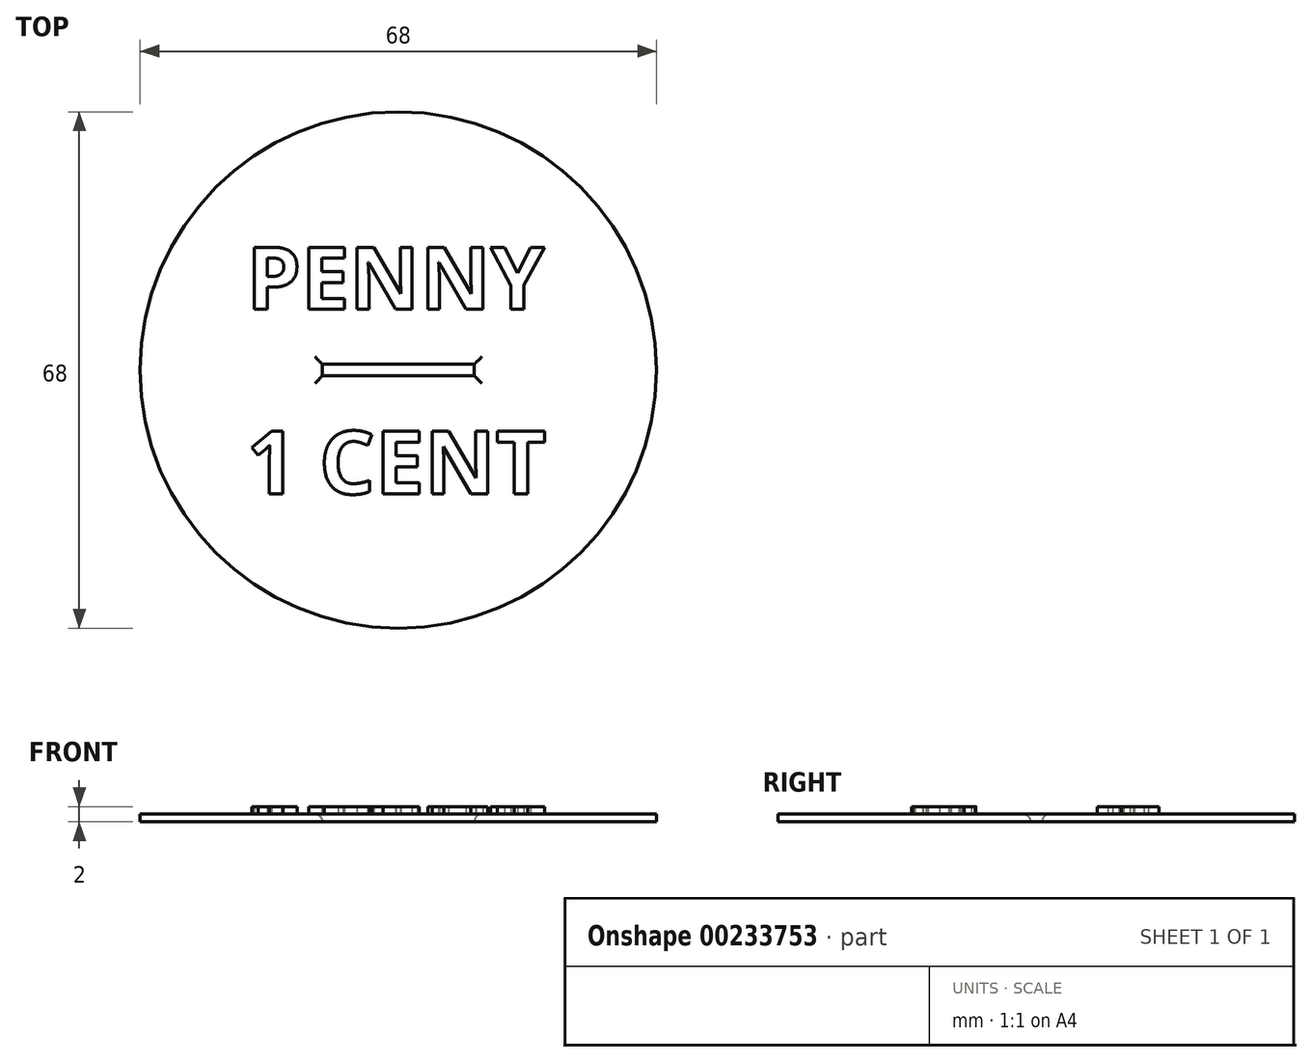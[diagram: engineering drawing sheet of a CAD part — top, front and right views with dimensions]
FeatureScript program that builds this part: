
annotation { "Feature Type Name" : "Feature", "Feature Type Description" : "" }
export const myFeature = defineFeature(function(context is Context, id is Id, definition is map)
    precondition{}
    {
        {
            var Q0;
            Q0=qCreatedBy(makeId("Front.planeOp"),FACE);
            var sketch = newSketch(context, id + "F0", { "sketchPlane" : qUnion([Q0])});
            skLineSegment(sketch, "E0", {"start": v(0, 0) * mm, "end": v(-34, 0) * mm});
            skLineSegment(sketch, "E1", {"start": v(-34, 1) * mm, "end": v(0, 1) * mm});
            skLineSegment(sketch, "E2", {"start": v(0, 0) * mm, "end": v(0, 1) * mm});
            skLineSegment(sketch, "E3", {"start": v(-34, 1) * mm, "end": v(-34, 0) * mm});
            skSolve(sketch);
        }
        {
            var Q0;
            Q0=makeQuery(id+"F0.imprint","IMPRINT",FACE,{"disambiguationData":[TD([[makeQuery(id+"F0.imprint","IMPRINT",EDGE,{"derivedFrom":sQuery(id+"F0.wireOp",EDGE,"E0")}),-1.0]])]});
            var Q1;
            Q1=sQuery(id+"F0.wireOp",EDGE,"E2");
            revolve(context, id + "F1", {"entities" : qUnion([Q0]), "axis" : qUnion([Q1]), "revolveType" : RevolveType.FULL});
        }
        {
            var Q0;
            Q0=qCreatedBy(makeId("Top.planeOp"),FACE);
            var sketch = newSketch(context, id + "F2", { "sketchPlane" : qUnion([Q0])});
            skLineSegment(sketch, "E4.bottom", {"start": v(10, 0.76) * mm, "end": v(-10, 0.76) * mm});
            skLineSegment(sketch, "E4.top", {"start": v(10, -0.76) * mm, "end": v(-10, -0.76) * mm});
            skLineSegment(sketch, "E4.left", {"start": v(10, 0.76) * mm, "end": v(10, -0.76) * mm});
            skLineSegment(sketch, "E4.right", {"start": v(-10, 0.76) * mm, "end": v(-10, -0.76) * mm});
            skPoint(sketch, "E4.middle", {"position": v(0, 0) * mm});
            skSolve(sketch);
        }
        {
            var Q0;
            Q0 = qSketchRegion(id + "F2", true);
            extrude(context, id + "F3", {"entities" : qUnion([Q0]), "operationType" : NewBodyOperationType.REMOVE, "endBound" : BoundingType.THROUGH_ALL, "depth" : 25 * mm});
        }
        {
            var Q0;
            Q0=makeQuery(id+"F3.boolean.opBoolean","INTERSECT",EDGE,{"derivedFrom":[makeQuery(id+"F1.opRevolve","SWEPT_FACE",FACE,{"disambiguationData":[OSD([sQuery(id+"F0.wireOp",EDGE,"E1")])]}),makeQuery(id+"F3.opExtrude","SWEPT_FACE",FACE,{"disambiguationData":[OSD([sQuery(id+"F2.wireOp",EDGE,"E4.bottom")])]})]});
            var Q1;
            Q1=makeQuery(id+"F3.boolean.opBoolean","INTERSECT",EDGE,{"derivedFrom":[makeQuery(id+"F1.opRevolve","SWEPT_FACE",FACE,{"disambiguationData":[OSD([sQuery(id+"F0.wireOp",EDGE,"E1")])]}),makeQuery(id+"F3.opExtrude","SWEPT_FACE",FACE,{"disambiguationData":[OSD([sQuery(id+"F2.wireOp",EDGE,"E4.right")])]})]});
            var Q2;
            Q2=makeQuery(id+"F3.boolean.opBoolean","INTERSECT",EDGE,{"derivedFrom":[makeQuery(id+"F1.opRevolve","SWEPT_FACE",FACE,{"disambiguationData":[OSD([sQuery(id+"F0.wireOp",EDGE,"E1")])]}),makeQuery(id+"F3.opExtrude","SWEPT_FACE",FACE,{"disambiguationData":[OSD([sQuery(id+"F2.wireOp",EDGE,"E4.top")])]})]});
            var Q3;
            Q3=makeQuery(id+"F3.boolean.opBoolean","INTERSECT",EDGE,{"derivedFrom":[makeQuery(id+"F1.opRevolve","SWEPT_FACE",FACE,{"disambiguationData":[OSD([sQuery(id+"F0.wireOp",EDGE,"E1")])]}),makeQuery(id+"F3.opExtrude","SWEPT_FACE",FACE,{"disambiguationData":[OSD([sQuery(id+"F2.wireOp",EDGE,"E4.left")])]})]});
            fillet(context, id + "F4", {"entities" : qUnion([Q0, Q1, Q2, Q3]), "radius" : 1 * mm, "tangentPropagation" : true, "allowEdgeOverflow" : false});
        }
        {
            var Q0;
            Q0=makeQuery(id+"F1.opRevolve","SWEPT_FACE",FACE,{"disambiguationData":[OSD([sQuery(id+"F0.wireOp",EDGE,"E1")])]});
            var sketch = newSketch(context, id + "F5", { "sketchPlane" : qUnion([Q0])});
            skText(sketch, "E5", { "text": "PENNY", "fontName": "OpenSans-Bold.ttf"});
            skText(sketch, "E6", { "text": "1 CENT", "fontName": "OpenSans-Bold.ttf"});
            const initialGuessF5  = {"E5": [-0.02, 0.008, 1, 0, 0.00822], "E6": [-0.02, -0.01631, 1, 0, 0.00831]};
            skSetInitialGuess(sketch, initialGuessF5);
            skSolve(sketch);
        }
        {
            var Q0;
            Q0 = qSketchRegion(id + "F5", true);
            extrude(context, id + "F6", {"entities" : qUnion([Q0]), "operationType" : NewBodyOperationType.ADD, "depth" : 1 * mm});
        }
    });
